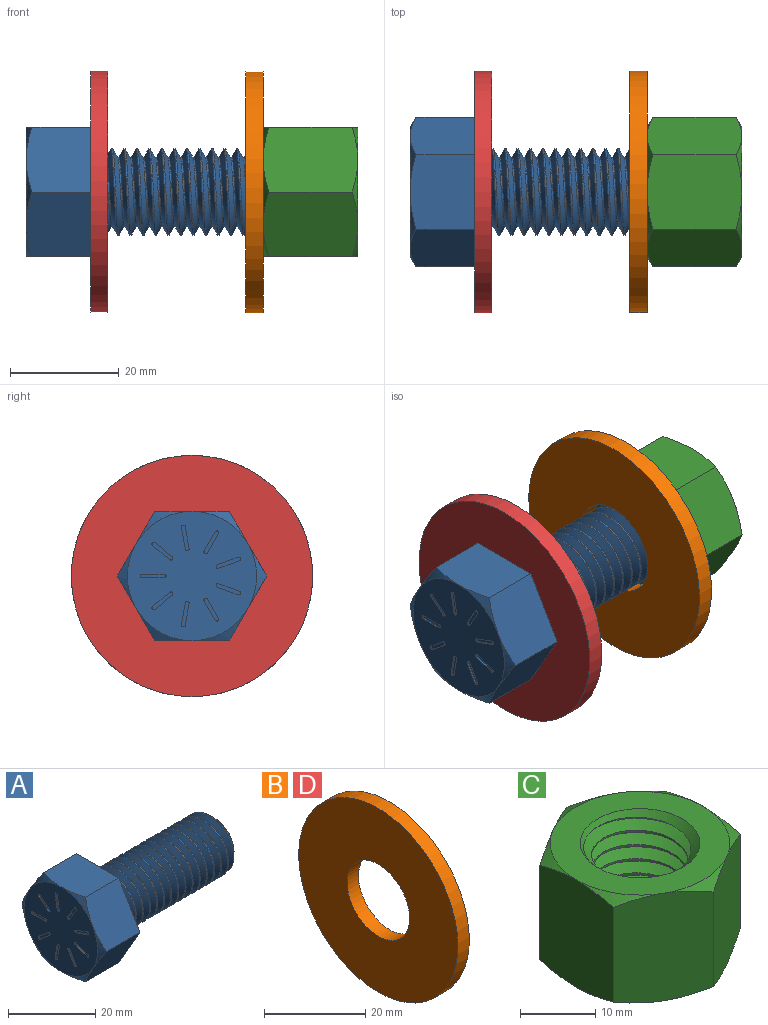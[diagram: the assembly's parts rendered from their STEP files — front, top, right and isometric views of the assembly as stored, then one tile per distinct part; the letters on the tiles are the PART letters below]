
ASSEMBLY  parts=4 mates=3
PART A: 65 faces, bbox 51.8x28.6x28.6 mm
  f0: plane 14.89x13.04mm, normal (0,0,1), area 158.7mm2, adj f1,f5,f12,f13,f18
  f1: plane 13.04x13.04mm, normal (0,0.87,0.5), area 158.7mm2, adj f0,f2,f12,f17,f18
  f2: plane 13.04x13.04mm, normal (0,0.87,-0.5), area 158.7mm2, adj f1,f3,f12,f16,f17
  f3: plane 14.89x13.04mm, normal (0,0,-1), area 158.7mm2, adj f2,f4,f12,f15,f16
  f4: plane 13.04x13.04mm, normal (0,-0.87,-0.5), area 158.7mm2, adj f3,f5,f12,f14,f15
  f5: plane 13.04x13.04mm, normal (0,-0.87,0.5), area 158.7mm2, adj f0,f4,f12,f13,f14
  f6: cylinder r=7.94mm len=36.37mm, axis (1,0,0), area 146.8mm2, adj f7,f10,f11,f12
  f7: cone r=6.21mm half-angle=45deg, axis (-1,0,0), area 59.7mm2, adj f6,f8,f9,f10,f11
  f8: plane 12.41x12.41mm, normal (1,0,0), area 121mm2, adj f7
  f9: bspline ~38.62x13.54mm, area 191.8mm2, adj f7,f10,f11,f12
  f10: bspline ~38.97x16.69mm, area 1257.3mm2, adj f6,f7,f9,f12
  f11: bspline ~39.6x15.87mm, area 1252.9mm2, adj f6,f7,f9,f12
  f12: plane 28.39x24.71mm, normal (1,0,0), area 327.9mm2, adj f0,f1,f2,f3,f4,f5,f6,f9
  f13: cone r=11.91mm half-angle=60deg, axis (1,0,0), area 13.9mm2, adj f0,f5,f19
  f14: cone r=11.91mm half-angle=60deg, axis (1,0,0), area 13.9mm2, adj f4,f5,f19
  f15: cone r=11.91mm half-angle=60deg, axis (1,0,0), area 13.9mm2, adj f3,f4,f19
  f16: cone r=11.91mm half-angle=60deg, axis (1,0,0), area 13.9mm2, adj f2,f3,f19
  f17: cone r=11.91mm half-angle=60deg, axis (1,0,0), area 13.9mm2, adj f1,f2,f19
  f18: cone r=11.91mm half-angle=60deg, axis (1,0,0), area 13.9mm2, adj f0,f1,f19
  f19: plane 23.81x23.81mm, normal (-1,0,0), area 415.7mm2, adj f13,f14,f15,f16,f17,f18,f20,f21
  f20: cylinder r=0.36mm len=0.71mm, axis (-1,0,0), area 0.3mm2, adj f19,f21,f23,f24
  f21: plane 4.05x0.25mm, normal (0,0,-1), area 1mm2, adj f19,f20,f22,f24
  f22: cylinder r=0.36mm len=0.71mm, axis (-1,0,0), area 0.3mm2, adj f19,f21,f23,f24
  f23: plane 4.05x0.25mm, normal (0,0,1), area 1mm2, adj f19,f20,f22,f24
  f24: plane 4.76x0.71mm, normal (-1,0,0), area 3.3mm2, adj f20,f21,f22,f23
  f25: cylinder r=0.36mm len=0.63mm, axis (-1,0,0), area 0.3mm2, adj f19,f26,f28,f29
  f26: plane 3.1x2.6mm, normal (0,0.64,-0.77), area 1mm2, adj f19,f25,f27,f29
  f27: cylinder r=0.36mm len=0.63mm, axis (-1,0,0), area 0.3mm2, adj f19,f26,f28,f29
  f28: plane 3.1x2.6mm, normal (0,-0.64,0.77), area 1mm2, adj f19,f25,f27,f29
  f29: plane 3.82x3.32mm, normal (-1,0,0), area 3.3mm2, adj f25,f26,f27,f28
  f30: cylinder r=0.36mm len=0.71mm, axis (-1,0,0), area 0.3mm2, adj f19,f31,f33,f34
  f31: plane 3.99x0.7mm, normal (0,0.98,-0.17), area 1mm2, adj f19,f30,f32,f34
  f32: cylinder r=0.36mm len=0.71mm, axis (-1,0,0), area 0.3mm2, adj f19,f31,f33,f34
  f33: plane 3.99x0.7mm, normal (0,-0.98,0.17), area 1mm2, adj f19,f30,f32,f34
  f34: plane 4.7x1.42mm, normal (-1,0,0), area 3.3mm2, adj f30,f31,f32,f33
  f35: cylinder r=0.36mm len=0.67mm, axis (-1,0,0), area 0.3mm2, adj f19,f36,f38,f39
  f36: plane 3.51x2.02mm, normal (0,0.87,0.5), area 1mm2, adj f19,f35,f37,f39
  f37: cylinder r=0.36mm len=0.67mm, axis (-1,0,0), area 0.3mm2, adj f19,f36,f38,f39
  f38: plane 3.51x2.02mm, normal (0,-0.87,-0.5), area 1mm2, adj f19,f35,f37,f39
  f39: plane 4.22x2.74mm, normal (-1,0,0), area 3.3mm2, adj f35,f36,f37,f38
  f40: cylinder r=0.36mm len=0.69mm, axis (-1,0,0), area 0.3mm2, adj f19,f41,f43,f44
  f41: plane 3.8x1.38mm, normal (0,0.34,0.94), area 1mm2, adj f19,f40,f42,f44
  f42: cylinder r=0.36mm len=0.69mm, axis (-1,0,0), area 0.3mm2, adj f19,f41,f43,f44
  f43: plane 3.8x1.38mm, normal (0,-0.34,-0.94), area 1mm2, adj f19,f40,f42,f44
  f44: plane 4.52x2.1mm, normal (-1,0,0), area 3.3mm2, adj f40,f41,f42,f43
  f45: cylinder r=0.36mm len=0.69mm, axis (-1,0,0), area 0.3mm2, adj f19,f46,f48,f49
  f46: plane 3.8x1.38mm, normal (0,-0.34,0.94), area 1mm2, adj f19,f45,f47,f49
  f47: cylinder r=0.36mm len=0.69mm, axis (-1,0,0), area 0.3mm2, adj f19,f46,f48,f49
  f48: plane 3.8x1.38mm, normal (0,0.34,-0.94), area 1mm2, adj f19,f45,f47,f49
  f49: plane 4.52x2.1mm, normal (-1,0,0), area 3.3mm2, adj f45,f46,f47,f48
  f50: cylinder r=0.36mm len=0.67mm, axis (-1,0,0), area 0.3mm2, adj f19,f51,f53,f54
  f51: plane 3.51x2.02mm, normal (0,-0.87,0.5), area 1mm2, adj f19,f50,f52,f54
  f52: cylinder r=0.36mm len=0.67mm, axis (-1,0,0), area 0.3mm2, adj f19,f51,f53,f54
  f53: plane 3.51x2.02mm, normal (0,0.87,-0.5), area 1mm2, adj f19,f50,f52,f54
  f54: plane 4.22x2.74mm, normal (-1,0,0), area 3.3mm2, adj f50,f51,f52,f53
  f55: cylinder r=0.36mm len=0.71mm, axis (-1,0,0), area 0.3mm2, adj f19,f56,f58,f59
  f56: plane 3.99x0.7mm, normal (0,-0.98,-0.17), area 1mm2, adj f19,f55,f57,f59
  f57: cylinder r=0.36mm len=0.71mm, axis (-1,0,0), area 0.3mm2, adj f19,f56,f58,f59
  f58: plane 3.99x0.7mm, normal (0,0.98,0.17), area 1mm2, adj f19,f55,f57,f59
  f59: plane 4.7x1.42mm, normal (-1,0,0), area 3.3mm2, adj f55,f56,f57,f58
  f60: cylinder r=0.36mm len=0.63mm, axis (-1,0,0), area 0.3mm2, adj f19,f61,f63,f64
  f61: plane 3.1x2.6mm, normal (0,-0.64,-0.77), area 1mm2, adj f19,f60,f62,f64
  f62: cylinder r=0.36mm len=0.63mm, axis (-1,0,0), area 0.3mm2, adj f19,f61,f63,f64
  f63: plane 3.1x2.6mm, normal (0,0.64,0.77), area 1mm2, adj f19,f60,f62,f64
  f64: plane 3.82x3.32mm, normal (-1,0,0), area 3.3mm2, adj f60,f61,f62,f63
PART B: 4 faces, bbox 3.2x44.5x44.5 mm
  f0: plane 44.45x44.45mm, normal (1,0,0), area 1312.3mm2, adj f2,f3
  f1: plane 44.45x44.45mm, normal (-1,0,0), area 1312.3mm2, adj f2,f3
  f2: cylinder r=22.23mm len=44.45mm, axis (-1,0,0), area 443.4mm2, adj f0,f1
  f3: cylinder r=8.73mm len=17.46mm, axis (-1,0,0), area 174.2mm2, adj f0,f1
PART C: 26 faces, bbox 28.6x28.6x20.3 mm
  f0: plane 23.81x23.81mm, normal (0,0,1), area 247.4mm2, adj f7,f12,f13,f14,f15,f16,f17,f18
  f1: plane 18.6x13.04mm, normal (-0.5,0.87,0), area 230mm2, adj f2,f6,f13,f18,f21,f22
  f2: plane 18.61x14.89mm, normal (-1,0,0), area 230mm2, adj f1,f3,f17,f18,f22,f23
  f3: plane 18.6x13.04mm, normal (-0.5,-0.87,0), area 230mm2, adj f2,f4,f16,f17,f23,f24
  f4: plane 18.6x13.04mm, normal (0.5,-0.87,0), area 230mm2, adj f3,f5,f15,f16,f24,f25
  f5: plane 18.61x14.89mm, normal (1,0,0), area 230mm2, adj f4,f6,f14,f15,f20,f25
  f6: plane 18.6x13.04mm, normal (0.5,0.87,0), area 230mm2, adj f1,f5,f13,f14,f20,f21
  f7: cylinder r=7.94mm len=17.46mm, axis (0,0,-1), area 110.5mm2, adj f0,f8,f9,f11
  f8: plane 23.81x23.81mm, normal (0,0,-1), area 247.4mm2, adj f7,f19,f20,f21,f22,f23,f24,f25
  f9: bspline ~18.33x15.83mm, area 542.8mm2, adj f7,f10,f12,f19
  f10: bspline ~15.3x13.54mm, area 73.1mm2, adj f9,f11,f12,f19
  f11: bspline ~18.42x16.69mm, area 543mm2, adj f7,f10,f12,f19
  f12: cone r=7.36mm half-angle=45deg, axis (0,0,1), area 49.1mm2, adj f0,f9,f10,f11
  f13: cone r=11.91mm half-angle=60deg, axis (0,0,-1), area 13.9mm2, adj f0,f1,f6
  f14: cone r=11.91mm half-angle=60deg, axis (0,0,-1), area 13.9mm2, adj f0,f5,f6
  f15: cone r=11.91mm half-angle=60deg, axis (0,0,-1), area 13.9mm2, adj f0,f4,f5
  f16: cone r=11.91mm half-angle=60deg, axis (0,0,-1), area 13.9mm2, adj f0,f3,f4
  f17: cone r=11.91mm half-angle=60deg, axis (0,0,-1), area 13.9mm2, adj f0,f2,f3
  f18: cone r=11.91mm half-angle=60deg, axis (0,0,-1), area 13.9mm2, adj f0,f1,f2
  f19: cone r=7.36mm half-angle=45deg, axis (0,0,-1), area 49.1mm2, adj f8,f9,f10,f11
  f20: cone r=11.91mm half-angle=60deg, axis (0,0,1), area 13.9mm2, adj f5,f6,f8
  f21: cone r=11.91mm half-angle=60deg, axis (0,0,1), area 13.9mm2, adj f1,f6,f8
  f22: cone r=11.91mm half-angle=60deg, axis (0,0,1), area 13.9mm2, adj f1,f2,f8
  f23: cone r=11.91mm half-angle=60deg, axis (0,0,1), area 13.9mm2, adj f2,f3,f8
  f24: cone r=11.91mm half-angle=60deg, axis (0,0,1), area 13.9mm2, adj f3,f4,f8
  f25: cone r=11.91mm half-angle=60deg, axis (0,0,1), area 13.9mm2, adj f4,f5,f8
PART D: same geometry as B
PLACE A t=(-53.59,30.71,92.47)mm
PLACE B t=(-38.11,30.71,92.47)mm
PLACE C rot(axis=(0.71,0,-0.71),180deg) t=(-26.2,30.71,92.47)mm
PLACE D rot(axis=(0,1,0),180deg) t=(-63.51,30.71,92.47)mm
MATE fastened C.f7 <-> B.f2  axis (-1,0,0) through (-34.94,30.71,92.47)mm
MATE fastened D.f2 <-> A.f6  axis (-1,0,0) through (-66.69,30.71,92.47)mm
MATE fastened B.f2 <-> D.f2  axis (-1,0,0) through (-38.11,30.71,92.47)mm
